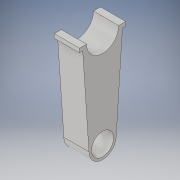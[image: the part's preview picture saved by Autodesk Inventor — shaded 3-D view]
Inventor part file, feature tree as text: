
AUTODESK INVENTOR PART (.ipt)
format: ipt  version: 2018 (Build 220112000, 112)  size: 178,688 bytes
history: native  units: in
note: dims shown in document units (in); Inventor stores cm internally (conversion verified against a paired STEP export)
features: extrude x8, sketch x8, plane x2, mirror x1, projected_geometry x1
ambient origin geometry x8: Origin, YZ Plane, XZ Plane, XY Plane, X Axis, Y Axis, Z Axis, Center Point
bodies: Solid1 (feature_tree)
feature tree (20):
  extrude  "Extrusion1"  Depth=2.5in TaperAngle=0.0deg
  extrude  "Extrusion2"  Depth=4.0in TaperAngle=0.0deg
  plane  "Work Plane1"
  extrude  "Extrusion3"  Depth=3.0in
  extrude  "Extrusion4"  Depth=1.0in
  extrude  "Extrusion5"  TaperAngle=0.0deg  [1 undecoded]
  extrude  "Extrusion6"  Depth=1.1in
  plane  "Work Plane2"
  extrude  "Extrusion7"  Depth=1.5in
  mirror  "Mirror1"
  extrude  "Extrusion8"  Depth=0.2in
  sketch  "Sketch1"  dims[d0=3.4in d1=2.5in d2=0.0in]
  sketch  "Sketch2"  dims[d4=1.5in d5=4.0in d6=0.0in]
  sketch  "Sketch3"  dims[d7=-2.5in d8=3.0in]
  sketch  "Sketch4"  dims[d9=2.25in d10=0.0in d11=1.0in]
  sketch  "Sketch5"  dims[d12=1.0in d13=0.0in]
  sketch  "Sketch6"  dims[d14=3.1in d15=0.0in d16=1.1in]
  sketch  "Sketch7"  dims[d17=1.35in d18=1.5in]
  sketch  "Sketch8"  dims[d19=1.7in d20=1.6in d21=0.0in d22=4.7in d23=2.0in d24=1.25in d25=0.0in d26=100.0in d27=0.0in d28=-0.9in d29=0.2in d30=0.25in d31=0.0in d32=1.5in d33=0.0in]
  projected_geometry  "Projected Loop1"
note: 1 required parameter value undecoded (feature->parameter linkage not recoverable at this tier; creation-order binding heuristic only, values carry confidence <= 0.55)
